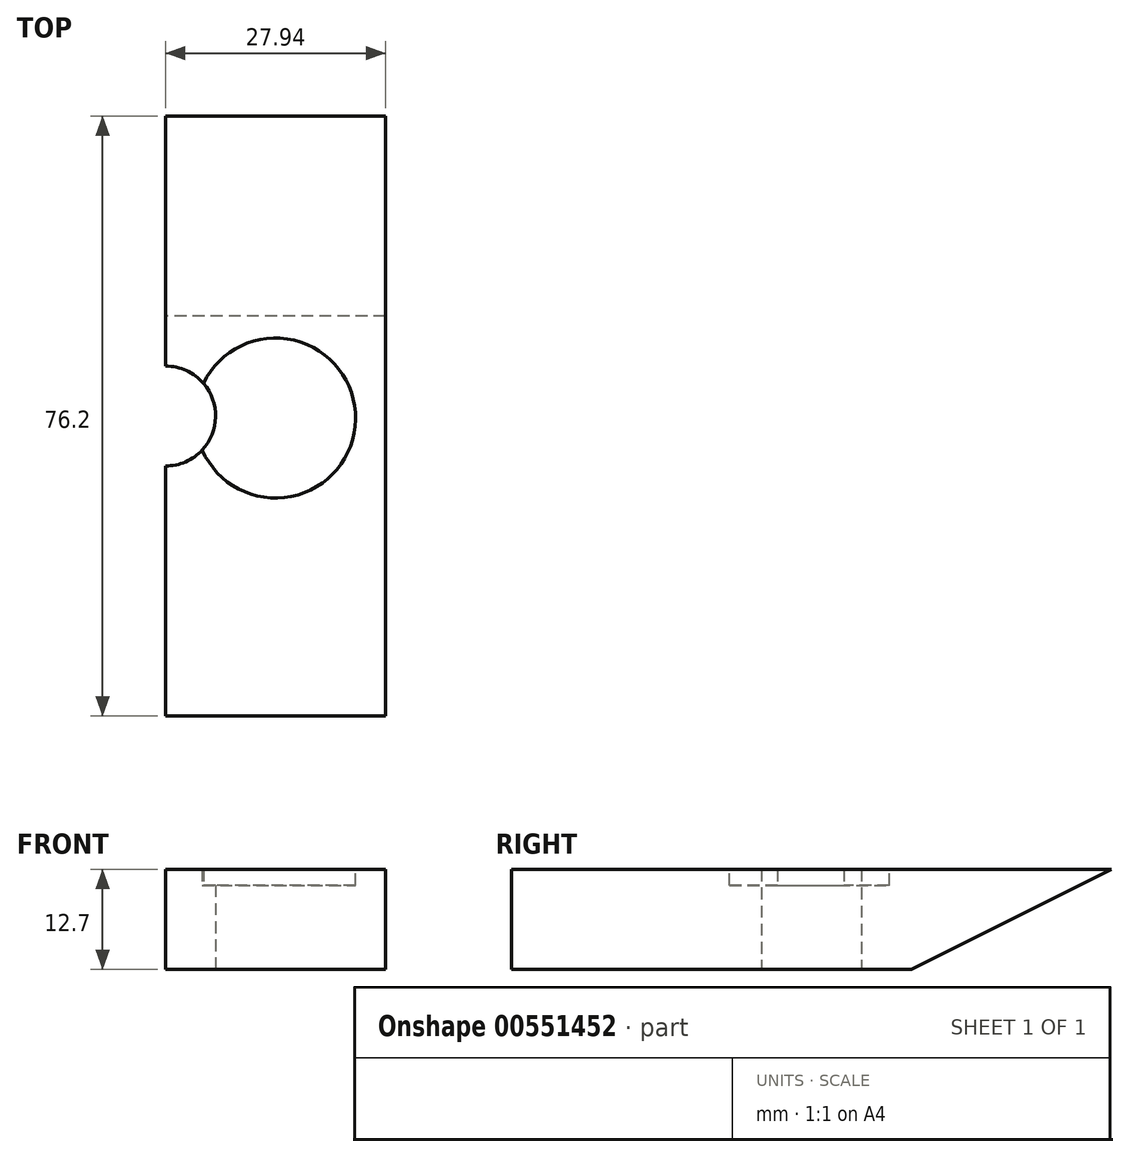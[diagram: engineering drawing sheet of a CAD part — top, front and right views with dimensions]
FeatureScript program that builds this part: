
annotation { "Feature Type Name" : "Feature", "Feature Type Description" : "" }
export const myFeature = defineFeature(function(context is Context, id is Id, definition is map)
    precondition{}
    {
        {
            var Q0;
            Q0=qCreatedBy(makeId("Right.planeOp"),FACE);
            var sketch = newSketch(context, id + "F0", { "sketchPlane" : qUnion([Q0])});
            skLineSegment(sketch, "E0", {"start": v(0, 0) * mm, "end": v(0, 12.7) * mm});
            skLineSegment(sketch, "E1", {"start": v(0, 12.7) * mm, "end": v(76.2, 12.7) * mm});
            skLineSegment(sketch, "E2", {"start": v(76.2, 12.7) * mm, "end": v(50.8, 0) * mm});
            skLineSegment(sketch, "E3", {"start": v(50.8, 0) * mm, "end": v(0, 0) * mm});
            skSolve(sketch);
        }
        {
            var Q0;
            Q0=qSketchRegion(id+"F0",true);
            extrude(context, id + "F1", {"entities" : qUnion([Q0]), "depth" : 27.94 * mm, "offsetDistance" : 25.4 * mm});
        }
        {
            var Q0;
            Q0=makeQuery(id+"F1.opExtrude","SWEPT_FACE",FACE,{"disambiguationData":[OSD([sQuery(id+"F0.wireOp",EDGE,"E1")])]});
            var sketch = newSketch(context, id + "F2", { "sketchPlane" : qUnion([Q0])});
            skCircle(sketch, "E4", {"center": v(13.97, 37.85) * mm, "radius": 10.16 * mm});
            skLineSegment(sketch, "E5", {"start": v(0, 76.2) * mm, "end": v(0, 48) * mm, "construction": true});
            skSolve(sketch);
        }
        {
            var Q0;
            Q0=qSketchRegion(id+"F2",true);
            extrude(context, id + "F3", {"entities" : qUnion([Q0]), "operationType" : NewBodyOperationType.REMOVE, "oppositeDirection" : true, "depth" : 2 * mm, "offsetDistance" : 25.4 * mm});
        }
        {
            var Q0;
            Q0=qCreatedBy(makeId("Top.planeOp"),FACE);
            var sketch = newSketch(context, id + "F4", { "sketchPlane" : qUnion([Q0])});
            skLineSegment(sketch, "E6", {"start": v(0, 0) * mm, "end": v(0, 76.2) * mm});
            skLineSegment(sketch, "E7", {"start": v(14.07, 38.1) * mm, "end": v(0, 38.1) * mm});
            skPoint(sketch, "E7.startSnap0", {"position": v(0, 38.1) * mm});
            skCircle(sketch, "E8", {"center": v(0, 38.1) * mm, "radius": 6.35 * mm});
            skSolve(sketch);
        }
        {
            var Q0;
            Q0 = qSketchRegion(id + "F4", true);
            extrude(context, id + "F5", {"entities" : qUnion([Q0]), "operationType" : NewBodyOperationType.REMOVE, "depth" : 25.4 * mm, "offsetDistance" : 25.4 * mm});
        }
    });
